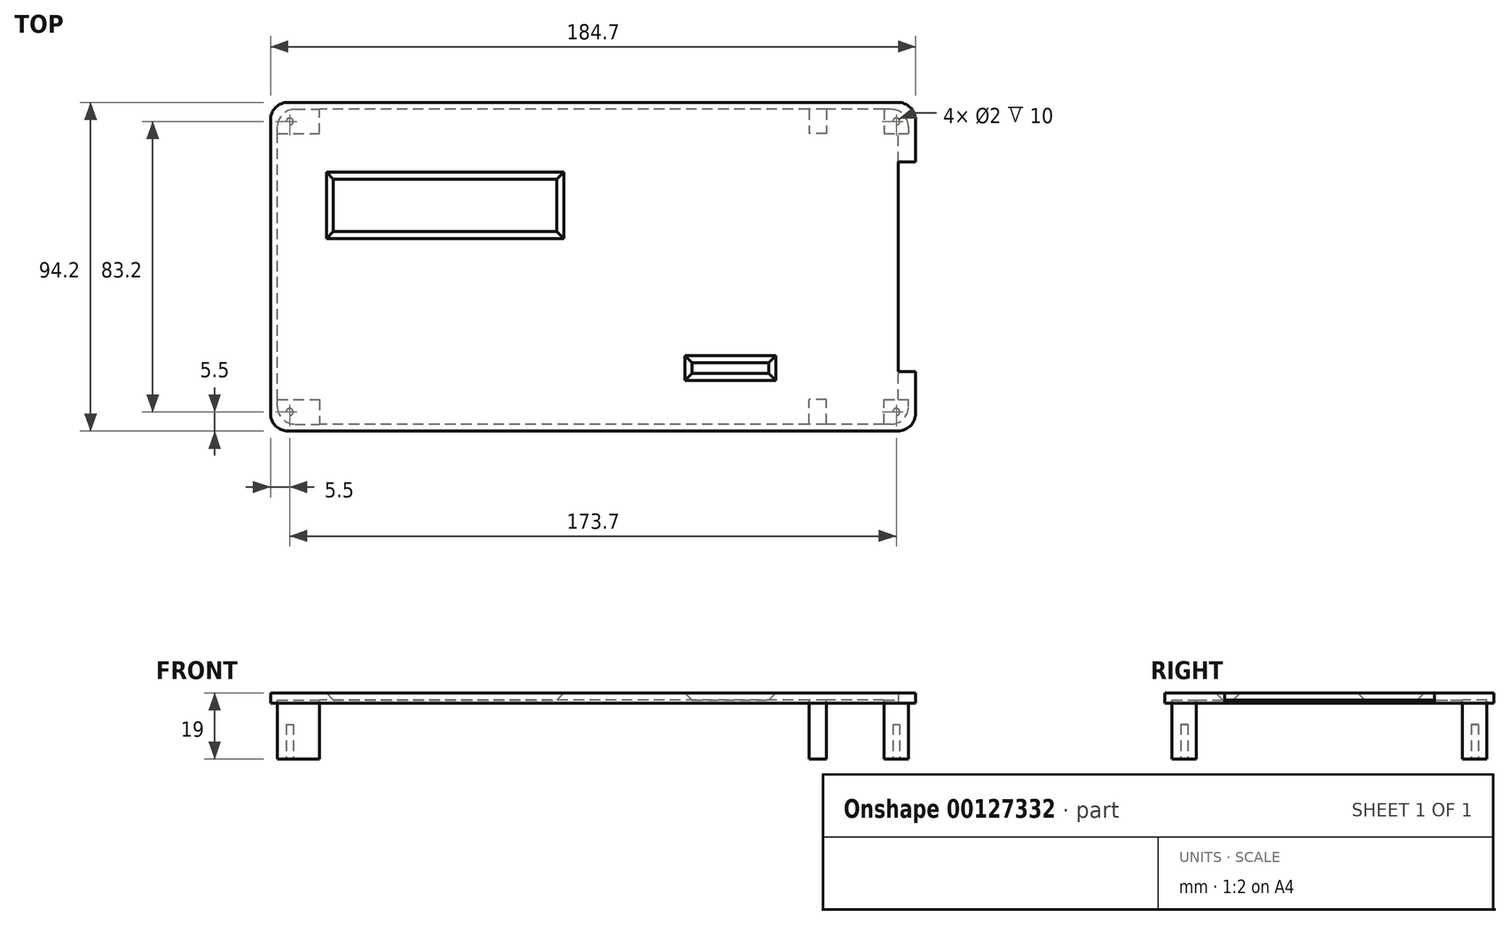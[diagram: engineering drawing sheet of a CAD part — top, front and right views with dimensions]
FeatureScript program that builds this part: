
annotation { "Feature Type Name" : "Feature", "Feature Type Description" : "" }
export const myFeature = defineFeature(function(context is Context, id is Id, definition is map)
    precondition{}
    {
        {
            var Q0;
            Q0=qCreatedBy(makeId("Top.planeOp"),FACE);
            var sketch = newSketch(context, id + "F0", { "sketchPlane" : qUnion([Q0])});
            skLineSegment(sketch, "E0.bottom", {"start": v(90.35, -45.1) * mm, "end": v(-90.35, -45.1) * mm});
            skLineSegment(sketch, "E0.top", {"start": v(90.35, 45.1) * mm, "end": v(-90.35, 45.1) * mm});
            skLineSegment(sketch, "E0.left", {"start": v(90.35, -45.1) * mm, "end": v(90.35, 45.1) * mm});
            skLineSegment(sketch, "E0.right", {"start": v(-90.35, -45.1) * mm, "end": v(-90.35, 45.1) * mm});
            skPoint(sketch, "E0.middle", {"position": v(0, 0) * mm});
            skSolve(sketch);
        }
        {
            var Q0;
            Q0=makeQuery(id+"F0.imprint","IMPRINT",FACE,{"disambiguationData":[TD([[makeQuery(id+"F0.imprint","IMPRINT",EDGE,{"derivedFrom":sQuery(id+"F0.wireOp",EDGE,"E0.bottom")}),-1.0]])]});
            extrude(context, id + "F1", {"entities" : qUnion([Q0]), "depth" : 2 * mm});
        }
        {
            var Q0;
            Q0=makeQuery(id+"F1.opExtrude","CAP_FACE",FACE,{"disambiguationData":[OSD([sQuery(id+"F0.wireOp",EDGE,"E0.bottom"),sQuery(id+"F0.wireOp",EDGE,"E0.top"),sQuery(id+"F0.wireOp",EDGE,"E0.left"),sQuery(id+"F0.wireOp",EDGE,"E0.right")])],"isStart":true});
            shell(context, id + "F2", {"entities" : qUnion([Q0]), "thickness" : 2 * mm, "oppositeDirection" : true});
        }
        {
            var Q0;
            Q0=makeQuery(id+"F1.opExtrude","CAP_FACE",FACE,{"disambiguationData":[OSD([sQuery(id+"F0.wireOp",EDGE,"E0.bottom"),sQuery(id+"F0.wireOp",EDGE,"E0.top"),sQuery(id+"F0.wireOp",EDGE,"E0.left"),sQuery(id+"F0.wireOp",EDGE,"E0.right")])],"isStart":true});
            extrude(context, id + "F3", {"entities" : qUnion([Q0]), "operationType" : NewBodyOperationType.REMOVE, "oppositeDirection" : true, "depth" : 1 * mm});
        }
        {
            var Q0;
            Q0=makeQuery(id+"F1.opExtrude","SWEPT_EDGE",EDGE,{"disambiguationData":[OSD([sQuery(id+"F0.wireOp",EDGE,"E0.bottom"),sQuery(id+"F0.wireOp",EDGE,"E0.right")])]});
            var Q1;
            Q1=makeQuery(id+"F1.opExtrude","SWEPT_EDGE",EDGE,{"disambiguationData":[OSD([sQuery(id+"F0.wireOp",EDGE,"E0.top"),sQuery(id+"F0.wireOp",EDGE,"E0.right")])]});
            var Q2;
            Q2=makeQuery(id+"F1.opExtrude","SWEPT_EDGE",EDGE,{"disambiguationData":[OSD([sQuery(id+"F0.wireOp",EDGE,"E0.bottom"),sQuery(id+"F0.wireOp",EDGE,"E0.left")])]});
            var Q3;
            Q3=makeQuery(id+"F1.opExtrude","SWEPT_EDGE",EDGE,{"disambiguationData":[OSD([sQuery(id+"F0.wireOp",EDGE,"E0.top"),sQuery(id+"F0.wireOp",EDGE,"E0.left")])]});
            var Q4;
            Q4=makeQuery(id+"F2.opShell","OFFSET_EDGE",EDGE,{"disambiguationData":[OSD([sQuery(id+"F0.wireOp",EDGE,"E0.top"),sQuery(id+"F0.wireOp",EDGE,"E0.right")])]});
            var Q5;
            Q5=makeQuery(id+"F2.opShell","OFFSET_EDGE",EDGE,{"disambiguationData":[OSD([sQuery(id+"F0.wireOp",EDGE,"E0.bottom"),sQuery(id+"F0.wireOp",EDGE,"E0.right")])]});
            var Q6;
            Q6=makeQuery(id+"F2.opShell","OFFSET_EDGE",EDGE,{"disambiguationData":[OSD([sQuery(id+"F0.wireOp",EDGE,"E0.top"),sQuery(id+"F0.wireOp",EDGE,"E0.left")])]});
            var Q7;
            Q7=makeQuery(id+"F2.opShell","OFFSET_EDGE",EDGE,{"disambiguationData":[OSD([sQuery(id+"F0.wireOp",EDGE,"E0.bottom"),sQuery(id+"F0.wireOp",EDGE,"E0.left")])]});
            fillet(context, id + "F4", {"entities" : qUnion([Q0, Q1, Q2, Q3, Q4, Q5, Q6, Q7]), "radius" : 5.08 * mm, "tangentPropagation" : true, "allowEdgeOverflow" : false});
        }
        {
            var Q0;
            Q0=makeQuery(id+"F1.opExtrude","CAP_FACE",FACE,{"disambiguationData":[OSD([sQuery(id+"F0.wireOp",EDGE,"E0.bottom"),sQuery(id+"F0.wireOp",EDGE,"E0.top"),sQuery(id+"F0.wireOp",EDGE,"E0.left"),sQuery(id+"F0.wireOp",EDGE,"E0.right")])],"isStart":false});
            var sketch = newSketch(context, id + "F5", { "sketchPlane" : qUnion([Q0])});
            skLineSegment(sketch, "E1.bottom", {"start": v(-8.35, 8.1) * mm, "end": v(-76.35, 8.1) * mm});
            skLineSegment(sketch, "E1.top", {"start": v(-8.35, 27.1) * mm, "end": v(-76.35, 27.1) * mm});
            skLineSegment(sketch, "E1.left", {"start": v(-8.35, 8.1) * mm, "end": v(-8.35, 27.1) * mm});
            skLineSegment(sketch, "E1.right", {"start": v(-76.35, 8.1) * mm, "end": v(-76.35, 27.1) * mm});
            skPoint(sketch, "E1.middle", {"position": v(-42.35, 17.6) * mm});
            skLineSegment(sketch, "E2", {"start": v(-42.35, 27.1) * mm, "end": v(-42.35, 47.1) * mm});
            skLineSegment(sketch, "E3", {"start": v(-76.35, 17.6) * mm, "end": v(-92.35, 17.6) * mm});
            skSolve(sketch);
        }
        {
            var Q0;
            Q0 = qSketchRegion(id + "F5", true);
            extrude(context, id + "F6", {"entities" : qUnion([Q0]), "operationType" : NewBodyOperationType.REMOVE, "endBound" : BoundingType.THROUGH_ALL, "oppositeDirection" : true, "depth" : 25 * mm, "hasDraft" : true, "draftAngle" : 45 * degree, "draftPullDirection" : true});
        }
        {
            var Q0;
            Q0=makeQuery(id+"F1.opExtrude","CAP_FACE",FACE,{"disambiguationData":[OSD([sQuery(id+"F0.wireOp",EDGE,"E0.bottom"),sQuery(id+"F0.wireOp",EDGE,"E0.top"),sQuery(id+"F0.wireOp",EDGE,"E0.left"),sQuery(id+"F0.wireOp",EDGE,"E0.right")])],"isStart":false});
            var sketch = newSketch(context, id + "F7", { "sketchPlane" : qUnion([Q0])});
            skLineSegment(sketch, "E4.bottom", {"start": v(4.35, 39.1) * mm, "end": v(74.35, 39.1) * mm});
            skLineSegment(sketch, "E4.top", {"start": v(4.35, -38.9) * mm, "end": v(74.35, -38.9) * mm});
            skLineSegment(sketch, "E4.left", {"start": v(4.35, 39.1) * mm, "end": v(4.35, -38.9) * mm});
            skLineSegment(sketch, "E4.right", {"start": v(74.35, 39.1) * mm, "end": v(74.35, -38.9) * mm});
            skLineSegment(sketch, "E5", {"start": v(74.35, 0) * mm, "end": v(92.35, 0) * mm});
            skPoint(sketch, "E5.startSnap0", {"position": v(92.35, 0) * mm});
            skLineSegment(sketch, "E6", {"start": v(39.35, 39.1) * mm, "end": v(39.35, 47.1) * mm});
            skLineSegment(sketch, "E7", {"start": v(39.35, -38.9) * mm, "end": v(39.35, -47.1) * mm});
            skLineSegment(sketch, "E8.bottom", {"start": v(52.35, -32.53) * mm, "end": v(26.35, -32.53) * mm});
            skLineSegment(sketch, "E8.top", {"start": v(52.35, -25.53) * mm, "end": v(26.35, -25.53) * mm});
            skLineSegment(sketch, "E8.left", {"start": v(52.35, -32.53) * mm, "end": v(52.35, -25.53) * mm});
            skLineSegment(sketch, "E8.right", {"start": v(26.35, -32.53) * mm, "end": v(26.35, -25.53) * mm});
            skPoint(sketch, "E8.middle", {"position": v(39.35, -29.03) * mm});
            skSolve(sketch);
        }
        {
            var Q0;
            Q0=makeQuery(id+"F7.imprint","IMPRINT",FACE,{"disambiguationData":[TD([[makeQuery(id+"F7.imprint","IMPRINT",EDGE,{"derivedFrom":sQuery(id+"F7.wireOp",EDGE,"E8.bottom")}),-1.0]])]});
            extrude(context, id + "F8", {"entities" : qUnion([Q0]), "operationType" : NewBodyOperationType.REMOVE, "endBound" : BoundingType.THROUGH_ALL, "oppositeDirection" : true, "depth" : 25 * mm, "hasDraft" : true, "draftAngle" : 45 * degree, "draftPullDirection" : true});
        }
        {
            var Q0;
            Q0=makeQuery(id+"F2.opShell","OFFSET_FACE",FACE,{"disambiguationData":[OSD([sQuery(id+"F0.wireOp",EDGE,"E0.bottom"),sQuery(id+"F0.wireOp",EDGE,"E0.top"),sQuery(id+"F0.wireOp",EDGE,"E0.left"),sQuery(id+"F0.wireOp",EDGE,"E0.right")])]});
            var sketch = newSketch(context, id + "F9", { "sketchPlane" : qUnion([Q0])});
            skLineSegment(sketch, "E9.bottom", {"start": v(83.35, 45.1) * mm, "end": v(90.35, 45.1) * mm});
            skLineSegment(sketch, "E9.top", {"start": v(83.35, 38.1) * mm, "end": v(90.35, 38.1) * mm});
            skLineSegment(sketch, "E9.left", {"start": v(83.35, 45.1) * mm, "end": v(83.35, 38.1) * mm});
            skLineSegment(sketch, "E9.right", {"start": v(90.35, 45.1) * mm, "end": v(90.35, 38.1) * mm});
            skLineSegment(sketch, "E10.bottom", {"start": v(83.35, -45.1) * mm, "end": v(90.35, -45.1) * mm});
            skLineSegment(sketch, "E10.top", {"start": v(83.35, -38.1) * mm, "end": v(90.35, -38.1) * mm});
            skLineSegment(sketch, "E10.left", {"start": v(83.35, -45.1) * mm, "end": v(83.35, -38.1) * mm});
            skLineSegment(sketch, "E10.right", {"start": v(90.35, -45.1) * mm, "end": v(90.35, -38.1) * mm});
            skLineSegment(sketch, "E11.bottom", {"start": v(-90.35, -38.1) * mm, "end": v(-83.35, -38.1) * mm});
            skLineSegment(sketch, "E11.top", {"start": v(-90.35, -45.1) * mm, "end": v(-83.35, -45.1) * mm});
            skLineSegment(sketch, "E11.left", {"start": v(-90.35, -38.1) * mm, "end": v(-90.35, -45.1) * mm});
            skLineSegment(sketch, "E11.right", {"start": v(-83.35, -38.1) * mm, "end": v(-83.35, -45.1) * mm});
            skLineSegment(sketch, "E12.bottom", {"start": v(-90.35, 38.1) * mm, "end": v(-83.35, 38.1) * mm});
            skLineSegment(sketch, "E12.top", {"start": v(-90.35, 45.1) * mm, "end": v(-83.35, 45.1) * mm});
            skLineSegment(sketch, "E12.left", {"start": v(-90.35, 38.1) * mm, "end": v(-90.35, 45.1) * mm});
            skLineSegment(sketch, "E12.right", {"start": v(-83.35, 38.1) * mm, "end": v(-83.35, 45.1) * mm});
            skSolve(sketch);
        }
        {
            var Q0;
            Q0 = qSketchRegion(id + "F9", true);
            extrude(context, id + "F10", {"entities" : qUnion([Q0]), "operationType" : NewBodyOperationType.ADD, "depth" : 17 * mm});
        }
        {
            var Q0;
            Q0=makeQuery(id+"F10.opExtrude","SWEPT_EDGE",EDGE,{"disambiguationData":[OSD([sQuery(id+"F9.wireOp",EDGE,"E12.top"),sQuery(id+"F9.wireOp",EDGE,"E12.left")])]});
            var Q1;
            Q1=makeQuery(id+"F10.opExtrude","SWEPT_EDGE",EDGE,{"disambiguationData":[OSD([sQuery(id+"F9.wireOp",EDGE,"E9.bottom"),sQuery(id+"F9.wireOp",EDGE,"E9.right")])]});
            var Q2;
            Q2=makeQuery(id+"F10.opExtrude","SWEPT_EDGE",EDGE,{"disambiguationData":[OSD([sQuery(id+"F9.wireOp",EDGE,"E10.bottom"),sQuery(id+"F9.wireOp",EDGE,"E10.right")])]});
            var Q3;
            Q3=makeQuery(id+"F10.opExtrude","SWEPT_EDGE",EDGE,{"disambiguationData":[OSD([sQuery(id+"F9.wireOp",EDGE,"E11.top"),sQuery(id+"F9.wireOp",EDGE,"E11.left")])]});
            fillet(context, id + "F11", {"entities" : qUnion([Q0, Q1, Q2, Q3]), "radius" : 5 * mm, "tangentPropagation" : true, "allowEdgeOverflow" : false});
        }
        {
            var Q0;
            Q0=makeQuery(id+"F10.opExtrude","CAP_FACE",FACE,{"disambiguationData":[OSD([sQuery(id+"F9.wireOp",EDGE,"E12.bottom"),sQuery(id+"F9.wireOp",EDGE,"E12.top"),sQuery(id+"F9.wireOp",EDGE,"E12.left"),sQuery(id+"F9.wireOp",EDGE,"E12.right")])],"isStart":false});
            var sketch = newSketch(context, id + "F12", { "sketchPlane" : qUnion([Q0])});
            skCircle(sketch, "E13", {"center": v(-86.85, 41.6) * mm, "radius": 1 * mm});
            skPoint(sketch, "E13.centerSnap0", {"position": v(-83.35, 41.6) * mm});
            skPoint(sketch, "E13.centerSnap1", {"position": v(-86.85, 38.1) * mm});
            skSolve(sketch);
        }
        {
            var Q0;
            Q0 = qSketchRegion(id + "F12", true);
            var Q1;
            Q1=makeQuery(id+"F12.imprint","IMPRINT",FACE,{"disambiguationData":[TD([[makeQuery(id+"F12.imprint","IMPRINT",EDGE,{"derivedFrom":sQuery(id+"F12.wireOp",EDGE,"E13")}),1.0]])]});
            extrude(context, id + "F13", {"entities" : qUnion([Q0, Q1]), "operationType" : NewBodyOperationType.REMOVE, "oppositeDirection" : true, "depth" : 10 * mm});
        }
        {
            var Q0;
            Q0=makeQuery(id+"F10.opExtrude","CAP_FACE",FACE,{"disambiguationData":[OSD([sQuery(id+"F9.wireOp",EDGE,"E11.bottom"),sQuery(id+"F9.wireOp",EDGE,"E11.top"),sQuery(id+"F9.wireOp",EDGE,"E11.left"),sQuery(id+"F9.wireOp",EDGE,"E11.right")])],"isStart":false});
            var sketch = newSketch(context, id + "F14", { "sketchPlane" : qUnion([Q0])});
            skCircle(sketch, "E14", {"center": v(-86.85, -41.6) * mm, "radius": 1 * mm});
            skPoint(sketch, "E14.centerSnap0", {"position": v(-86.85, -38.1) * mm});
            skPoint(sketch, "E14.centerSnap1", {"position": v(-83.35, -41.6) * mm});
            skSolve(sketch);
        }
        {
            var Q0;
            Q0 = qSketchRegion(id + "F14", true);
            var Q1;
            Q1=makeQuery(id+"F14.imprint","IMPRINT",FACE,{"disambiguationData":[TD([[makeQuery(id+"F14.imprint","IMPRINT",EDGE,{"derivedFrom":sQuery(id+"F14.wireOp",EDGE,"E14")}),1.0]])]});
            extrude(context, id + "F15", {"entities" : qUnion([Q0, Q1]), "operationType" : NewBodyOperationType.REMOVE, "oppositeDirection" : true, "depth" : 10 * mm});
        }
        {
            var Q0;
            Q0=makeQuery(id+"F10.opExtrude","CAP_FACE",FACE,{"disambiguationData":[OSD([sQuery(id+"F9.wireOp",EDGE,"E10.bottom"),sQuery(id+"F9.wireOp",EDGE,"E10.top"),sQuery(id+"F9.wireOp",EDGE,"E10.left"),sQuery(id+"F9.wireOp",EDGE,"E10.right")])],"isStart":false});
            var sketch = newSketch(context, id + "F16", { "sketchPlane" : qUnion([Q0])});
            skCircle(sketch, "E15", {"center": v(86.85, -41.6) * mm, "radius": 1 * mm});
            skPoint(sketch, "E15.centerSnap0", {"position": v(83.35, -41.6) * mm});
            skPoint(sketch, "E15.centerSnap1", {"position": v(86.85, -38.1) * mm});
            skSolve(sketch);
        }
        {
            var Q0;
            Q0=makeQuery(id+"F16.imprint","IMPRINT",FACE,{"disambiguationData":[TD([[makeQuery(id+"F16.imprint","IMPRINT",EDGE,{"derivedFrom":sQuery(id+"F16.wireOp",EDGE,"E15")}),1.0]])]});
            extrude(context, id + "F17", {"entities" : qUnion([Q0]), "operationType" : NewBodyOperationType.REMOVE, "oppositeDirection" : true, "depth" : 10 * mm});
        }
        {
            var Q0;
            Q0=makeQuery(id+"F10.opExtrude","CAP_FACE",FACE,{"disambiguationData":[OSD([sQuery(id+"F9.wireOp",EDGE,"E9.bottom"),sQuery(id+"F9.wireOp",EDGE,"E9.top"),sQuery(id+"F9.wireOp",EDGE,"E9.left"),sQuery(id+"F9.wireOp",EDGE,"E9.right")])],"isStart":false});
            var sketch = newSketch(context, id + "F18", { "sketchPlane" : qUnion([Q0])});
            skCircle(sketch, "E16", {"center": v(86.85, 41.6) * mm, "radius": 1 * mm});
            skPoint(sketch, "E16.centerSnap0", {"position": v(83.35, 41.6) * mm});
            skPoint(sketch, "E16.centerSnap1", {"position": v(86.85, 38.1) * mm});
            skSolve(sketch);
        }
        {
            var Q0;
            Q0=makeQuery(id+"F18.imprint","IMPRINT",FACE,{"disambiguationData":[TD([[makeQuery(id+"F18.imprint","IMPRINT",EDGE,{"derivedFrom":sQuery(id+"F18.wireOp",EDGE,"E16")}),1.0]])]});
            extrude(context, id + "F19", {"entities" : qUnion([Q0]), "operationType" : NewBodyOperationType.REMOVE, "oppositeDirection" : true, "depth" : 10 * mm});
        }
        {
            var Q0;
            Q0=makeQuery(id+"F10.opExtrude","SWEPT_FACE",FACE,{"disambiguationData":[OSD([sQuery(id+"F9.wireOp",EDGE,"E12.right")])]});
            extrude(context, id + "F20", {"entities" : qUnion([Q0]), "operationType" : NewBodyOperationType.ADD, "depth" : 5 * mm});
        }
        {
            var Q0;
            Q0=makeQuery(id+"F10.opExtrude","SWEPT_FACE",FACE,{"disambiguationData":[OSD([sQuery(id+"F9.wireOp",EDGE,"E11.right")])]});
            extrude(context, id + "F21", {"entities" : qUnion([Q0]), "operationType" : NewBodyOperationType.ADD, "depth" : 5 * mm});
        }
        {
            var Q0;
            Q0=makeQuery(id+"F2.opShell","OFFSET_FACE",FACE,{"disambiguationData":[OSD([sQuery(id+"F0.wireOp",EDGE,"E0.left")])]});
            extrude(context, id + "F22", {"entities" : qUnion([Q0]), "operationType" : NewBodyOperationType.ADD, "depth" : 3 * mm});
        }
        {
            var Q0;
            {var subQ0=sQuery(id+"F0.wireOp",EDGE,"E0.left");Q0=makeQuery(id+"F22.boolean.opBoolean","MERGE",FACE,{"derivedFrom":[makeQuery(id+"F3.boolean.opBoolean","COPY",FACE,{"derivedFrom":makeQuery(id+"F3.opExtrude","CAP_FACE",FACE,{"disambiguationData":[OSD([sQuery(id+"F0.wireOp",EDGE,"E0.bottom"),sQuery(id+"F0.wireOp",EDGE,"E0.top"),subQ0,sQuery(id+"F0.wireOp",EDGE,"E0.right")])],"isStart":false})}),makeQuery(id+"F22.opExtrude","SWEPT_FACE",FACE,{"disambiguationData":[OSD([subQ0]),TDD([makeQuery(id+"F10.boolean.opBoolean","SPLIT",EDGE,{"derivedFrom":makeQuery(id+"F3.boolean.opBoolean","COPY",EDGE,{"derivedFrom":makeQuery(id+"F3.opExtrude","CAP_EDGE",EDGE,{"disambiguationData":[OSD([subQ0]),TDD([makeQuery(id+"F2.opShell","OFFSET_EDGE",EDGE,{"disambiguationData":[OSD([subQ0]),TDD([makeQuery(id+"F1.opExtrude","CAP_EDGE",EDGE,{"disambiguationData":[OSD([subQ0])],"isStart":true})])]})])],"isStart":false})})})])]})]});}
            var sketch = newSketch(context, id + "F23", { "sketchPlane" : qUnion([Q0])});
            skLineSegment(sketch, "E17.bottom", {"start": v(87.35, 30) * mm, "end": v(92.35, 30) * mm});
            skLineSegment(sketch, "E17.top", {"start": v(87.35, -30) * mm, "end": v(92.35, -30) * mm});
            skLineSegment(sketch, "E17.left", {"start": v(87.35, 30) * mm, "end": v(87.35, -30) * mm});
            skLineSegment(sketch, "E17.right", {"start": v(92.35, 30) * mm, "end": v(92.35, -30) * mm});
            skLineSegment(sketch, "E18", {"start": v(87.35, 38.1) * mm, "end": v(87.35, 30) * mm});
            skLineSegment(sketch, "E19", {"start": v(87.35, -38.1) * mm, "end": v(87.35, -30) * mm});
            skPoint(sketch, "E20.oppositeSnap0", {"position": v(87.35, 34.05) * mm});
            skLineSegment(sketch, "E21.bottom", {"start": v(88.85, -30) * mm, "end": v(90.35, -30) * mm});
            skLineSegment(sketch, "E21.top", {"start": v(88.85, -33) * mm, "end": v(90.35, -33) * mm});
            skLineSegment(sketch, "E21.left", {"start": v(88.85, -30) * mm, "end": v(88.85, -33) * mm});
            skLineSegment(sketch, "E21.right", {"start": v(90.35, -30) * mm, "end": v(90.35, -33) * mm});
            skLineSegment(sketch, "E22.bottom", {"start": v(88.85, 30) * mm, "end": v(90.35, 30) * mm});
            skLineSegment(sketch, "E22.top", {"start": v(88.85, 33) * mm, "end": v(90.35, 33) * mm});
            skLineSegment(sketch, "E22.left", {"start": v(88.85, 30) * mm, "end": v(88.85, 33) * mm});
            skLineSegment(sketch, "E22.right", {"start": v(90.35, 30) * mm, "end": v(90.35, 33) * mm});
            skLineSegment(sketch, "E23", {"start": v(90.35, 33) * mm, "end": v(92.35, 33) * mm});
            skLineSegment(sketch, "E24", {"start": v(90.35, -33) * mm, "end": v(92.35, -33) * mm});
            skSolve(sketch);
        }
        {
            var Q0;
            {var subQ5=sQuery(id+"F23.wireOp",EDGE,"E17.left");Q0=makeQuery(id+"F23.imprint","IMPRINT",FACE,{"disambiguationData":[TD([[makeQuery(id+"F23.imprint","IMPRINT",EDGE,{"derivedFrom":subQ5}),1.0]])]});}
            var Q1;
            Q1=makeQuery(id+"F23.imprint","IMPRINT",FACE,{"disambiguationData":[TD([[makeQuery(id+"F23.imprint","IMPRINT",EDGE,{"derivedFrom":sQuery(id+"F23.wireOp",EDGE,"E22.bottom")}),1.0]])]});
            var Q2;
            Q2=makeQuery(id+"F23.imprint","IMPRINT",FACE,{"disambiguationData":[TD([[makeQuery(id+"F23.imprint","IMPRINT",EDGE,{"derivedFrom":sQuery(id+"F23.wireOp",EDGE,"E21.bottom")}),-1.0]])]});
            extrude(context, id + "F24", {"entities" : qUnion([Q0, Q1, Q2]), "operationType" : NewBodyOperationType.REMOVE, "endBound" : BoundingType.THROUGH_ALL, "oppositeDirection" : true, "depth" : 25 * mm});
        }
        {
            var Q0;
            Q0=makeQuery(id+"F2.opShell","OFFSET_FACE",FACE,{"disambiguationData":[OSD([sQuery(id+"F0.wireOp",EDGE,"E0.bottom"),sQuery(id+"F0.wireOp",EDGE,"E0.top"),sQuery(id+"F0.wireOp",EDGE,"E0.left"),sQuery(id+"F0.wireOp",EDGE,"E0.right")])]});
            var sketch = newSketch(context, id + "F25", { "sketchPlane" : qUnion([Q0])});
            skLineSegment(sketch, "E25.bottom", {"start": v(66.85, 45.1) * mm, "end": v(68.35, 45.1) * mm});
            skLineSegment(sketch, "E25.top", {"start": v(66.85, -45.1) * mm, "end": v(68.35, -45.1) * mm});
            skLineSegment(sketch, "E25.left", {"start": v(66.85, 45.1) * mm, "end": v(66.85, -45.1) * mm});
            skLineSegment(sketch, "E25.right", {"start": v(68.35, 45.1) * mm, "end": v(68.35, -45.1) * mm});
            skLineSegment(sketch, "E26", {"start": v(87.35, 0) * mm, "end": v(68.35, 0) * mm});
            skSolve(sketch);
        }
        {
            var Q0;
            Q0=makeQuery(id+"F2.opShell","OFFSET_FACE",FACE,{"disambiguationData":[OSD([sQuery(id+"F0.wireOp",EDGE,"E0.bottom"),sQuery(id+"F0.wireOp",EDGE,"E0.top"),sQuery(id+"F0.wireOp",EDGE,"E0.left"),sQuery(id+"F0.wireOp",EDGE,"E0.right")])]});
            var sketch = newSketch(context, id + "F26", { "sketchPlane" : qUnion([Q0])});
            skLineSegment(sketch, "E27.bottom", {"start": v(66.85, 45.1) * mm, "end": v(61.85, 45.1) * mm});
            skLineSegment(sketch, "E27.top", {"start": v(66.85, 38.1) * mm, "end": v(61.85, 38.1) * mm});
            skLineSegment(sketch, "E27.left", {"start": v(66.85, 45.1) * mm, "end": v(66.85, 38.1) * mm});
            skLineSegment(sketch, "E27.right", {"start": v(61.85, 45.1) * mm, "end": v(61.85, 38.1) * mm});
            skLineSegment(sketch, "E28.bottom", {"start": v(66.85, -45.1) * mm, "end": v(61.85, -45.1) * mm});
            skLineSegment(sketch, "E28.top", {"start": v(66.85, -38.1) * mm, "end": v(61.85, -38.1) * mm});
            skLineSegment(sketch, "E28.left", {"start": v(66.85, -45.1) * mm, "end": v(66.85, -38.1) * mm});
            skLineSegment(sketch, "E28.right", {"start": v(61.85, -45.1) * mm, "end": v(61.85, -38.1) * mm});
            skSolve(sketch);
        }
        {
            var Q0;
            Q0=makeQuery(id+"F26.imprint","IMPRINT",FACE,{"disambiguationData":[TD([[makeQuery(id+"F26.imprint","IMPRINT",EDGE,{"derivedFrom":sQuery(id+"F26.wireOp",EDGE,"E27.bottom")}),1.0]])]});
            var Q1;
            Q1=makeQuery(id+"F26.imprint","IMPRINT",FACE,{"disambiguationData":[TD([[makeQuery(id+"F26.imprint","IMPRINT",EDGE,{"derivedFrom":sQuery(id+"F26.wireOp",EDGE,"E28.bottom")}),-1.0]])]});
            extrude(context, id + "F27", {"entities" : qUnion([Q0, Q1]), "operationType" : NewBodyOperationType.ADD, "depth" : 17 * mm});
        }
    });
